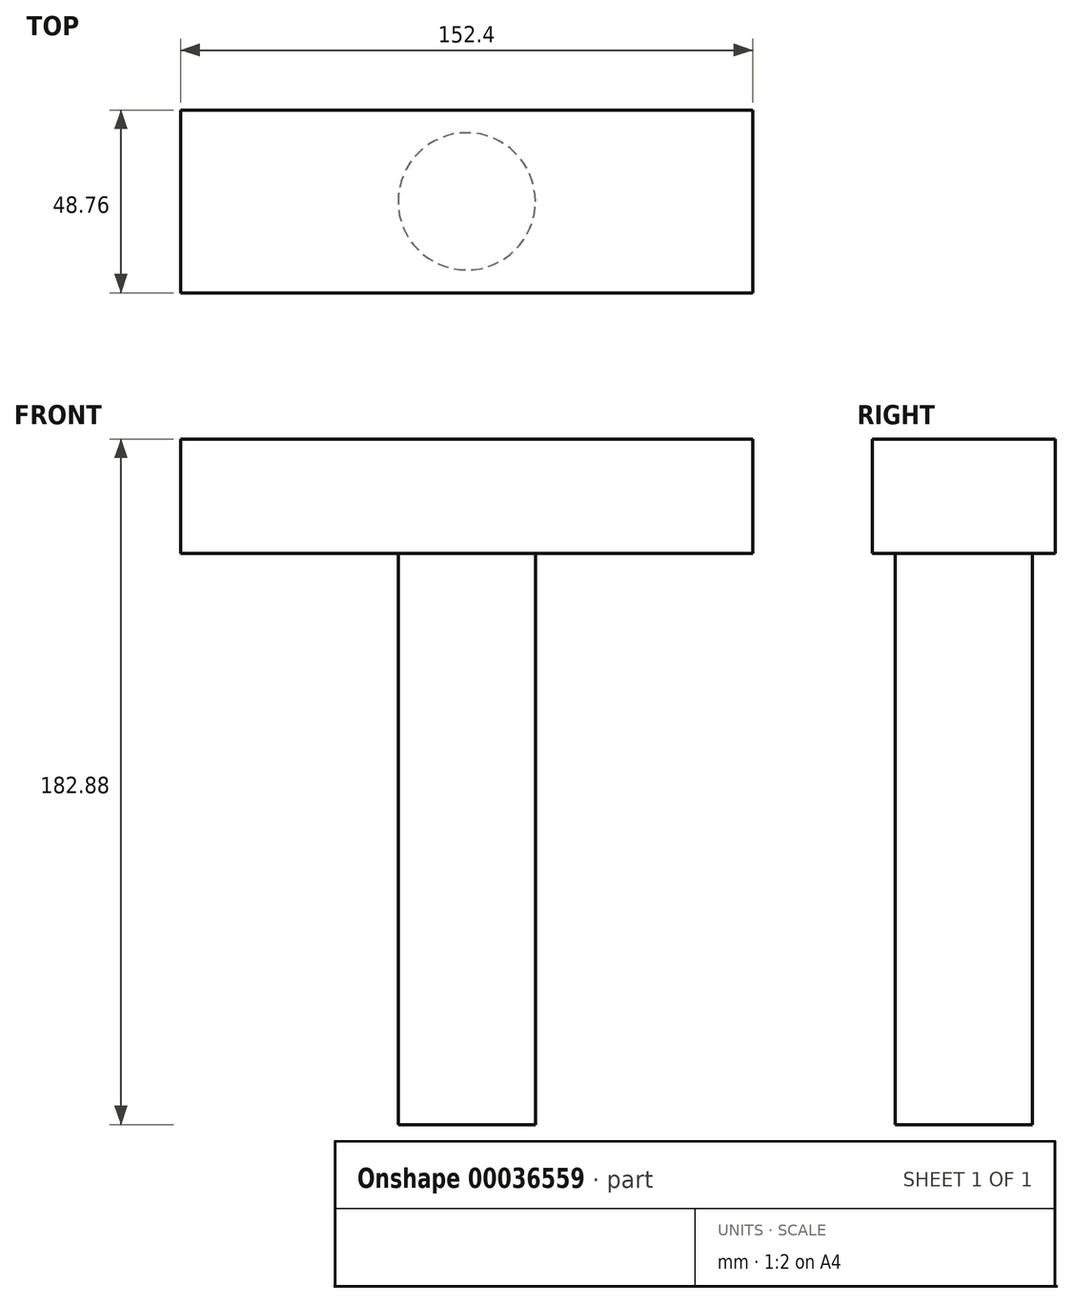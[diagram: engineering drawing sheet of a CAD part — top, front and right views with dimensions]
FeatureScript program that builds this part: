
annotation { "Feature Type Name" : "Feature", "Feature Type Description" : "" }
export const myFeature = defineFeature(function(context is Context, id is Id, definition is map)
    precondition{}
    {
        {
            var Q0;
            Q0=qCreatedBy(makeId("Top.planeOp"),FACE);
            var sketch = newSketch(context, id + "F0", { "sketchPlane" : qUnion([Q0])});
            skCircle(sketch, "E0", {"center": v(0, 0) * mm, "radius": 18.29 * mm});
            skSolve(sketch);
        }
        {
            var Q0;
            Q0 = qSketchRegion(id + "F0", true);
            extrude(context, id + "F1", {"entities" : qUnion([Q0]), "depth" : 152.4 * mm});
        }
        {
            var Q0;
            Q0=makeQuery(id+"F1.opExtrude","CAP_FACE",FACE,{"disambiguationData":[OSD([sQuery(id+"F0.wireOp",EDGE,"E0")])],"isStart":false});
            var sketch = newSketch(context, id + "F2", { "sketchPlane" : qUnion([Q0])});
            skLineSegment(sketch, "E1.rect.bottom", {"start": v(-76.2, 24.38) * mm, "end": v(76.2, 24.38) * mm});
            skLineSegment(sketch, "E1.rect.top", {"start": v(-76.2, -24.38) * mm, "end": v(76.2, -24.38) * mm});
            skLineSegment(sketch, "E1.rect.left", {"start": v(-76.2, 24.38) * mm, "end": v(-76.2, -24.38) * mm});
            skLineSegment(sketch, "E1.rect.right", {"start": v(76.2, 24.38) * mm, "end": v(76.2, -24.38) * mm});
            skPoint(sketch, "E1.rect.middle", {"position": v(0, 0) * mm});
            skSolve(sketch);
        }
        {
            var Q0;
            Q0 = qSketchRegion(id + "F2", true);
            extrude(context, id + "F3", {"entities" : qUnion([Q0]), "operationType" : NewBodyOperationType.ADD, "depth" : 30.48 * mm});
        }
    });
